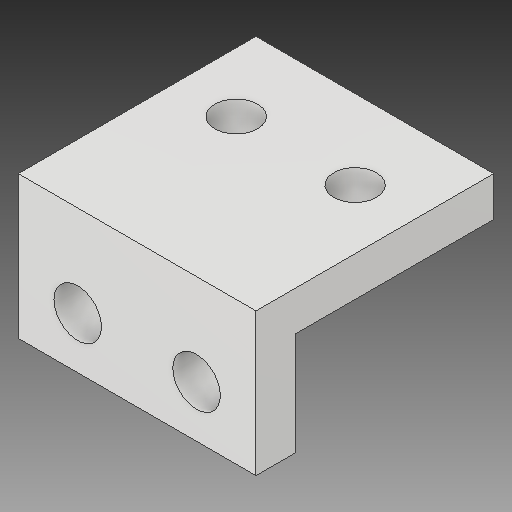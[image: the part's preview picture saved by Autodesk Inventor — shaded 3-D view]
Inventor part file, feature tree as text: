
AUTODESK INVENTOR PART (.ipt)
format: ipt  version: 2017 (Build 210142000, 142)  size: 116,736 bytes
history: native  units: in
note: dims shown in document units (in); Inventor stores cm internally (conversion verified against a paired STEP export)
features: other x3, sketch x3
ambient origin geometry x8: Origin, YZ Plane, XZ Plane, XY Plane, X Axis, Y Axis, Z Axis, Center Point
bodies: Solid1 (feature_tree)
feature tree (6):
  other  "TensionerPlate4a.ipt"
  other  "Solid1::TensionerPlate4a.ipt"
  other  "TaggingFeature1"
  sketch  "Sketch1"  dims[d0=0.3937in]
  sketch  "Sketch2"
  sketch  "Sketch3"
